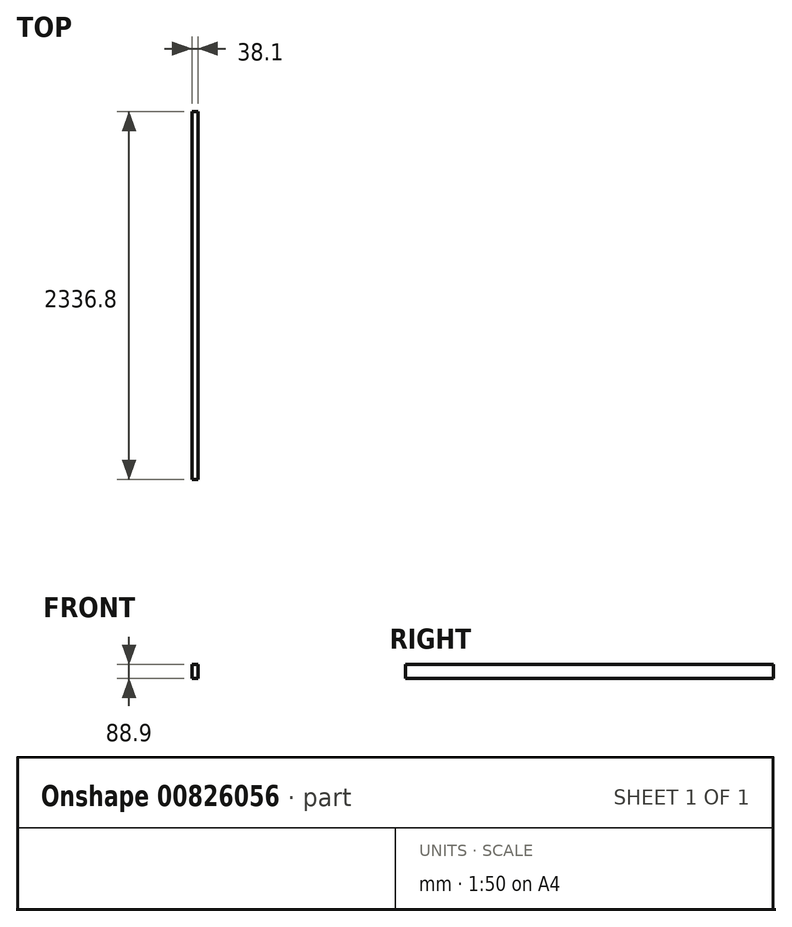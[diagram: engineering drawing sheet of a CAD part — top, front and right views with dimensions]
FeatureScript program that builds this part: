
annotation { "Feature Type Name" : "Feature", "Feature Type Description" : "" }
export const myFeature = defineFeature(function(context is Context, id is Id, definition is map)
    precondition{}
    {
        {
            var Q0;
            Q0=qCreatedBy(makeId("Front.planeOp"),FACE);
            var sketch = newSketch(context, id + "F0", { "sketchPlane" : qUnion([Q0])});
            skLineSegment(sketch, "E0.bottom", {"start": v(-19.05, 44.45) * mm, "end": v(19.05, 44.45) * mm});
            skLineSegment(sketch, "E0.top", {"start": v(-19.05, -44.45) * mm, "end": v(19.05, -44.45) * mm});
            skLineSegment(sketch, "E0.left", {"start": v(-19.05, 44.45) * mm, "end": v(-19.05, -44.45) * mm});
            skLineSegment(sketch, "E0.right", {"start": v(19.05, 44.45) * mm, "end": v(19.05, -44.45) * mm});
            skPoint(sketch, "E0.middle", {"position": v(0, 0) * mm});
            skSolve(sketch);
        }
        {
            var Q0;
            Q0=makeQuery(id+"F0.imprint","IMPRINT",FACE,{"disambiguationData":[TD([[makeQuery(id+"F0.imprint","IMPRINT",EDGE,{"derivedFrom":sQuery(id+"F0.wireOp",EDGE,"E0.bottom")}),-1.0]])]});
            extrude(context, id + "F1", {"entities" : qUnion([Q0]), "endBound" : BoundingType.SYMMETRIC, "depth" : 2336.8 * mm, "offsetDistance" : 25.4 * mm});
        }
    });
